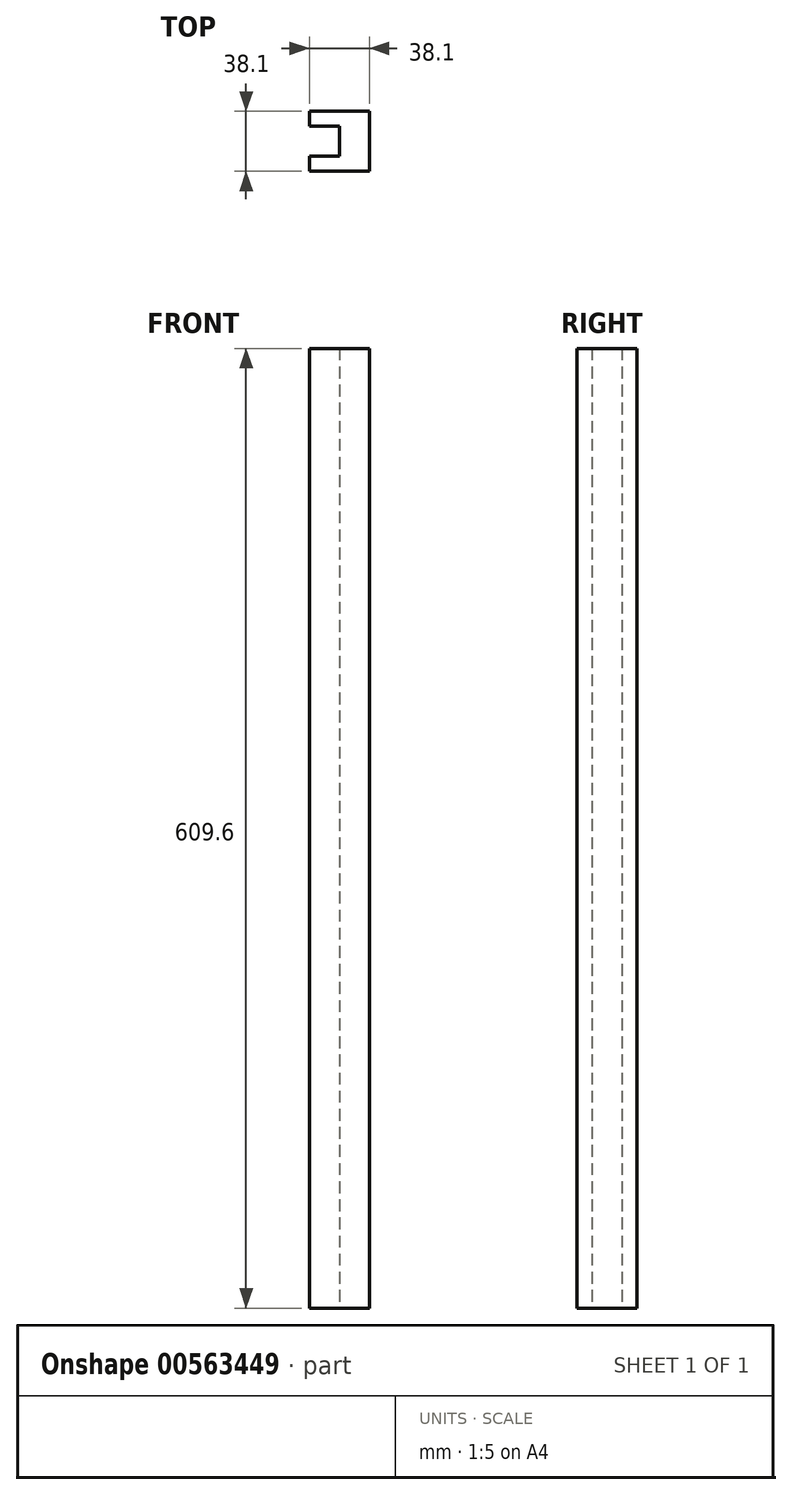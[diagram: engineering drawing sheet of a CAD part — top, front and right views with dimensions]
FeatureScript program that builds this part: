
annotation { "Feature Type Name" : "Feature", "Feature Type Description" : "" }
export const myFeature = defineFeature(function(context is Context, id is Id, definition is map)
    precondition{}
    {
        {
            var Q0;
            Q0=qCreatedBy(makeId("Top.planeOp"),FACE);
            var sketch = newSketch(context, id + "F0", { "sketchPlane" : qUnion([Q0])});
            skLineSegment(sketch, "E0", {"start": v(-16.7, 10.37) * mm, "end": v(-16.7, 0.85) * mm});
            skLineSegment(sketch, "E1", {"start": v(-16.7, 0.85) * mm, "end": v(2.35, 0.85) * mm});
            skLineSegment(sketch, "E2", {"start": v(2.35, 0.85) * mm, "end": v(2.35, -18.2) * mm});
            skLineSegment(sketch, "E3", {"start": v(2.35, -18.2) * mm, "end": v(-16.7, -18.2) * mm});
            skLineSegment(sketch, "E4", {"start": v(-16.7, -18.2) * mm, "end": v(-16.7, -27.73) * mm});
            skLineSegment(sketch, "E5", {"start": v(-16.7, -27.73) * mm, "end": v(21.4, -27.73) * mm});
            skLineSegment(sketch, "E6", {"start": v(21.4, -27.73) * mm, "end": v(21.4, 10.37) * mm});
            skLineSegment(sketch, "E7", {"start": v(21.4, 10.37) * mm, "end": v(-16.7, 10.37) * mm});
            skSolve(sketch);
        }
        {
            var Q0;
            Q0=qSketchRegion(id+"F0",true);
            extrude(context, id + "F1", {"entities" : qUnion([Q0]), "depth" : 609.6 * mm, "offsetDistance" : 25.4 * mm});
        }
    });
